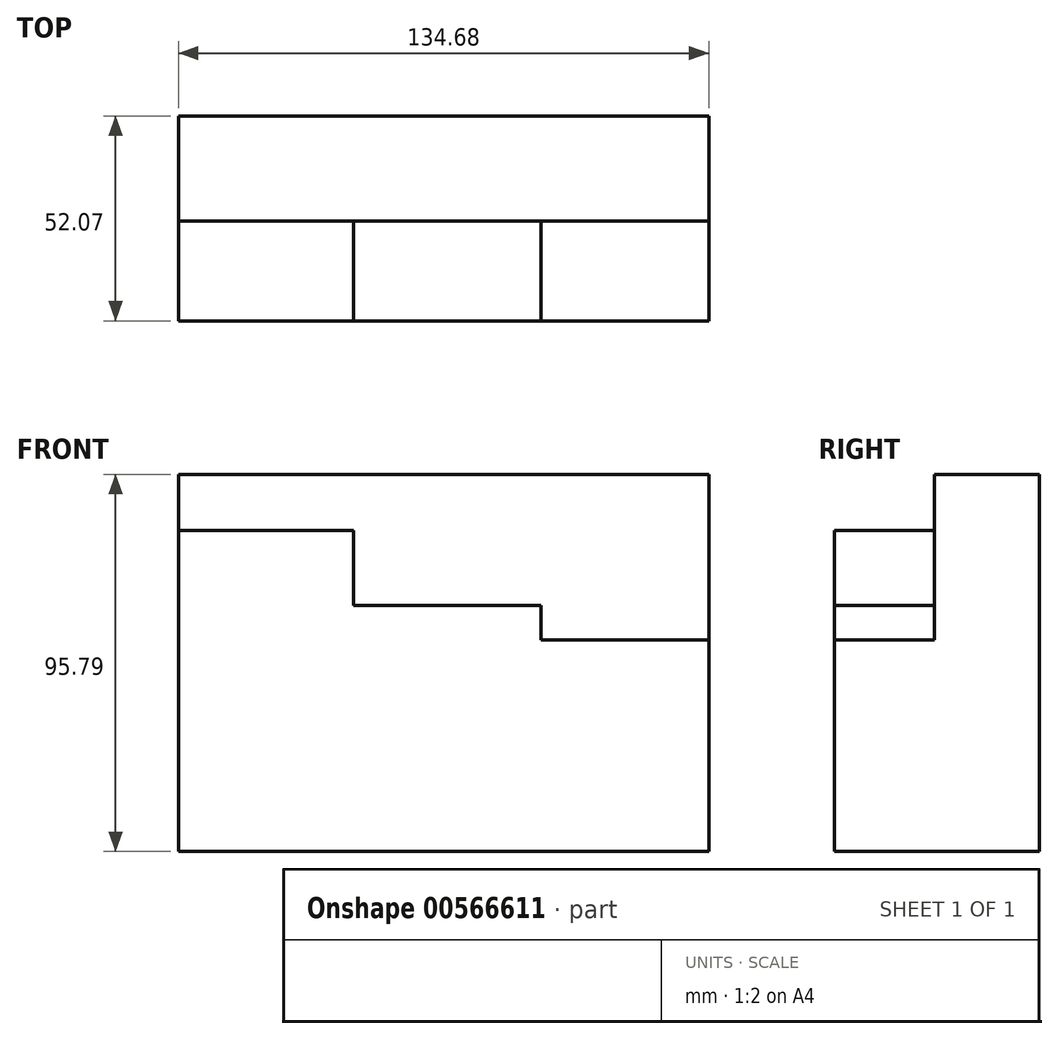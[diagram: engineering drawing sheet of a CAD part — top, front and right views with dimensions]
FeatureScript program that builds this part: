
annotation { "Feature Type Name" : "Feature", "Feature Type Description" : "" }
export const myFeature = defineFeature(function(context is Context, id is Id, definition is map)
    precondition{}
    {
        {
            var Q0;
            Q0=qCreatedBy(makeId("Front.planeOp"),FACE);
            var sketch = newSketch(context, id + "F0", { "sketchPlane" : qUnion([Q0])});
            skLineSegment(sketch, "E0.bottom", {"start": v(66.12, 49.23) * mm, "end": v(-68.56, 49.23) * mm});
            skLineSegment(sketch, "E0.top", {"start": v(66.12, -46.56) * mm, "end": v(-68.56, -46.56) * mm});
            skLineSegment(sketch, "E0.left", {"start": v(66.12, 49.23) * mm, "end": v(66.12, -46.56) * mm});
            skLineSegment(sketch, "E0.right", {"start": v(-68.56, 49.23) * mm, "end": v(-68.56, -46.56) * mm});
            skSolve(sketch);
        }
        {
            var Q0;
            Q0 = qSketchRegion(id + "F0", true);
            extrude(context, id + "F1", {"entities" : qUnion([Q0]), "oppositeDirection" : true, "depth" : 26.67 * mm, "offsetDistance" : 25.4 * mm});
        }
        {
            var Q0;
            Q0=makeQuery(id+"F1.opExtrude","CAP_FACE",FACE,{"disambiguationData":[OSD([sQuery(id+"F0.wireOp",EDGE,"E0.bottom"),sQuery(id+"F0.wireOp",EDGE,"E0.top"),sQuery(id+"F0.wireOp",EDGE,"E0.left"),sQuery(id+"F0.wireOp",EDGE,"E0.right")])],"isStart":true});
            var sketch = newSketch(context, id + "F2", { "sketchPlane" : qUnion([Q0])});
            skLineSegment(sketch, "E1.bottom", {"start": v(-68.56, 35) * mm, "end": v(-24.11, 35) * mm});
            skLineSegment(sketch, "E1.top", {"start": v(-68.56, -46.56) * mm, "end": v(-24.11, -46.56) * mm});
            skLineSegment(sketch, "E1.left", {"start": v(-68.56, 35) * mm, "end": v(-68.56, -46.56) * mm});
            skLineSegment(sketch, "E1.right", {"start": v(-24.11, 35) * mm, "end": v(-24.11, -46.56) * mm});
            skLineSegment(sketch, "E2.bottom", {"start": v(-24.11, 15.9) * mm, "end": v(23.45, 15.9) * mm});
            skLineSegment(sketch, "E2.top", {"start": v(-24.11, -46.56) * mm, "end": v(23.45, -46.56) * mm});
            skLineSegment(sketch, "E2.right", {"start": v(23.45, 15.9) * mm, "end": v(23.45, -46.56) * mm});
            skLineSegment(sketch, "E3.bottom", {"start": v(23.45, 7.22) * mm, "end": v(66.12, 7.22) * mm});
            skLineSegment(sketch, "E3.top", {"start": v(23.45, -46.56) * mm, "end": v(66.12, -46.56) * mm});
            skLineSegment(sketch, "E3.left", {"start": v(23.45, 7.22) * mm, "end": v(23.45, -46.56) * mm});
            skLineSegment(sketch, "E3.right", {"start": v(66.12, 7.22) * mm, "end": v(66.12, -46.56) * mm});
            skSolve(sketch);
        }
        {
            var Q0;
            Q0 = qSketchRegion(id + "F2", true);
            extrude(context, id + "F3", {"entities" : qUnion([Q0]), "operationType" : NewBodyOperationType.ADD, "depth" : 25.4 * mm, "offsetDistance" : 25.4 * mm});
        }
    });
